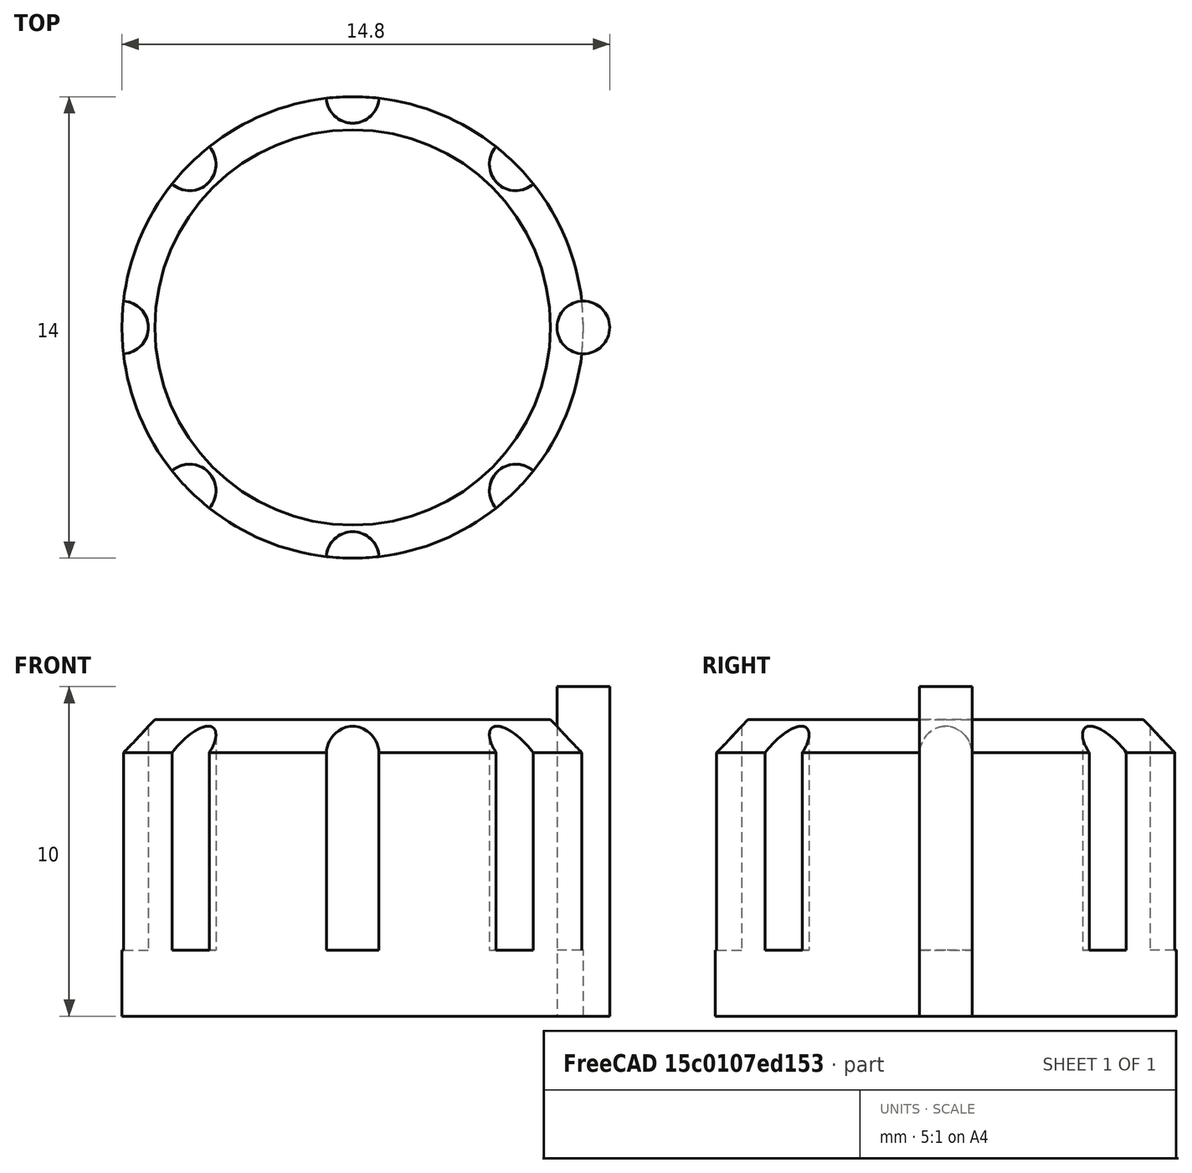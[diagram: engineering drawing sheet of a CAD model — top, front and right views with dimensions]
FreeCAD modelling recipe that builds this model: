
FCSTD DOCUMENT  (FreeCAD 0.21R33694 (Git))
Label: OJT1_T011_botò
License: All rights reserved
LicenseURL: https://en.wikipedia.org/wiki/All_rights_reserved
objects: Part::Cylinder×2, Part::Chamfer×1, Part::FeaturePython×1, Part::Cut×1
note: 4 computed .brp shape members not serialized (recipe doc carries the construction recipe); baked Part::Feature solids carry a one-line shape summary decoded from their .brp

FEATURE [Part::Cylinder] Cylinder  label="Cilindre"
  Angle = 360
  AttacherType = Attacher::AttachEngine3D
  FirstAngle = 0
  Height = 9
  Radius = 7
  SecondAngle = 0
FEATURE [Part::Chamfer] Chamfer
  Base = -> Cylinder
  Edges = 1 edges r=1: [Edge3]
FEATURE [Part::Cylinder] Cylinder001  label="Cilindre001"
  Angle = 360
  AttacherType = Attacher::AttachEngine3D
  FirstAngle = 0
  Height = 10
  Placement = pos=(7,0,0) rot=(0,0,1;0rad)
  Radius = 0.8
  SecondAngle = 0
FEATURE [Part::FeaturePython] Array  # Draft array (typed FeaturePython)
  AlwaysSyncPlacement = false
  Angle = 360
  ArrayType = 1
  Axis = (0,0,1)
  Base = -> Cylinder001
  Center = (0,0,0)
  Count = 8
  ExpandArray = false
  Fuse = false
  IntervalAxis = (0,0,0)
  IntervalX = (100,0,0)
  IntervalY = (0,100,0)
  IntervalZ = (0,0,100)
  NumberCircles = 3
  NumberPolar = 8
  NumberX = 2
  NumberY = 2
  NumberZ = 1
  Placement = pos=(0,0,2) rot=(0,0,1;0rad)
  PlacementList = 8 placements: [(7,0,0),(4.94975,4.94975,0),(0,7,0),(-4.94975,4.94975,0),(-7,8.57253e-16,0),(-4.94975,-4.94975,0),(-1.55431e-15,-7,0),(4.94975,-4.94975,0)]
  RadialDistance = 50
  ScaleList = (8) [(1,1,1),(1,1,1),(1,1,1),(1,1,1),(1,1,1),(1,1,1),(1,1,1),(1,1,1)]
  Symmetry = 1
  TangentialDistance = 25
FEATURE [Part::Cut] Cut
  Base = -> Chamfer
  Tool = -> Array
